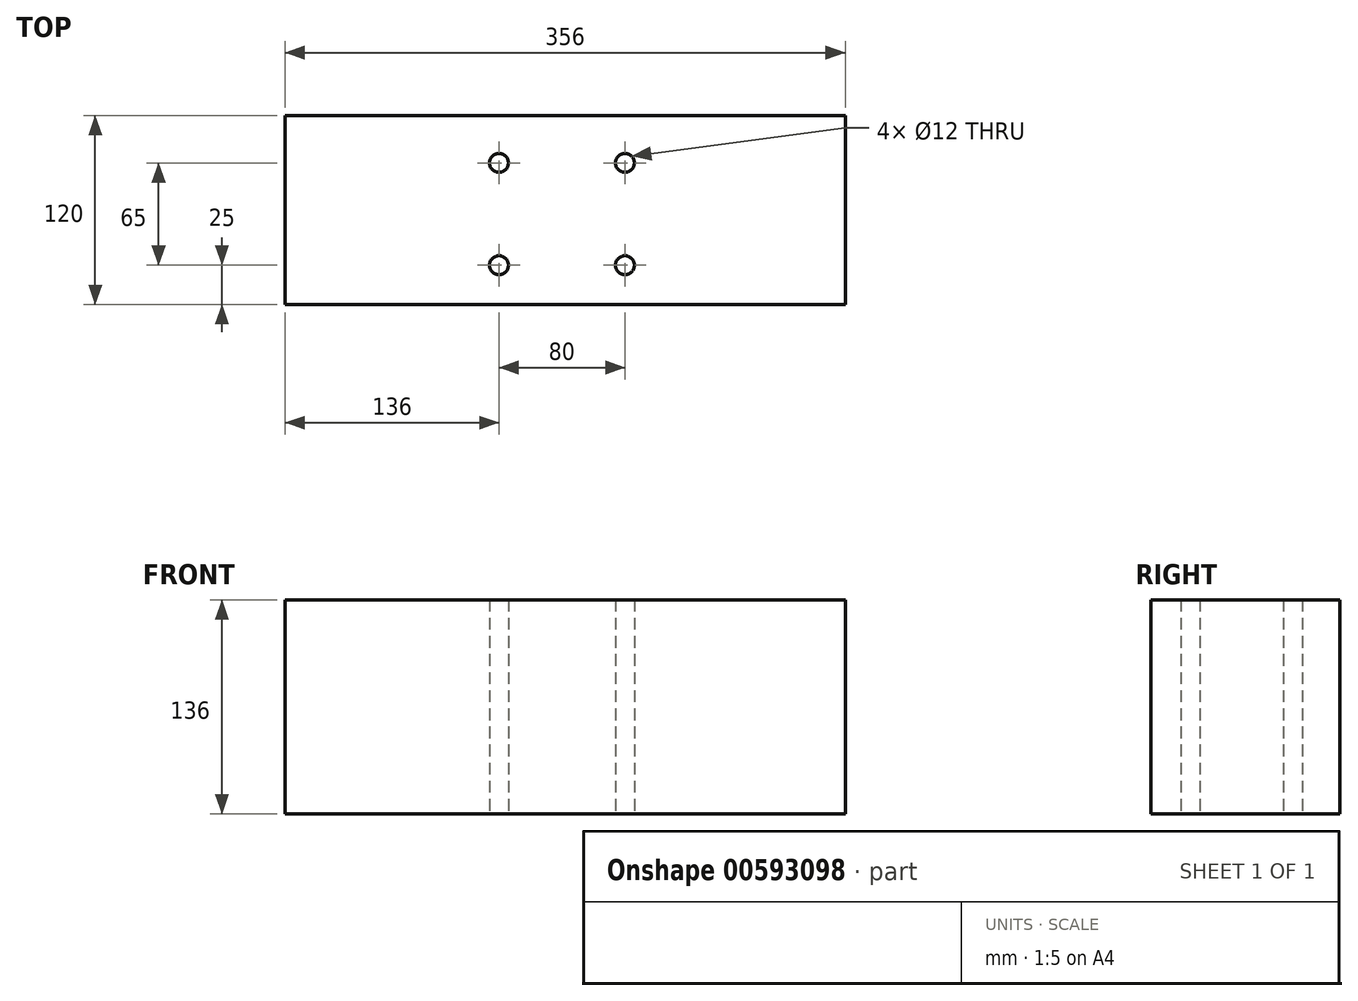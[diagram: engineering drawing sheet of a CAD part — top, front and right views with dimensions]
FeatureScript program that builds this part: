
annotation { "Feature Type Name" : "Feature", "Feature Type Description" : "" }
export const myFeature = defineFeature(function(context is Context, id is Id, definition is map)
    precondition{}
    {
        {
            var Q0;
            Q0=qCreatedBy(makeId("Top.planeOp"),FACE);
            var sketch = newSketch(context, id + "F0", { "sketchPlane" : qUnion([Q0])});
            skLineSegment(sketch, "E0.bottom", {"start": v(178, 60) * mm, "end": v(-178, 60) * mm});
            skLineSegment(sketch, "E0.top", {"start": v(178, -60) * mm, "end": v(-178, -60) * mm});
            skLineSegment(sketch, "E0.left", {"start": v(178, 60) * mm, "end": v(178, -60) * mm});
            skLineSegment(sketch, "E0.right", {"start": v(-178, 60) * mm, "end": v(-178, -60) * mm});
            skPoint(sketch, "E0.middle", {"position": v(0, 0) * mm});
            skCircle(sketch, "E1", {"center": v(-42, 30) * mm, "radius": 6 * mm});
            skCircle(sketch, "E2", {"center": v(38, 30) * mm, "radius": 6 * mm});
            skCircle(sketch, "E3", {"center": v(38, -35) * mm, "radius": 6 * mm});
            skCircle(sketch, "E4", {"center": v(-42, -35) * mm, "radius": 6 * mm});
            skSolve(sketch);
        }
        {
            var Q0;
            Q0=makeQuery(id+"F0.imprint","IMPRINT",FACE,{"disambiguationData":[TD([[makeQuery(id+"F0.imprint","IMPRINT",EDGE,{"derivedFrom":sQuery(id+"F0.wireOp",EDGE,"E0.bottom")}),1.0]])]});
            extrude(context, id + "F1", {"entities" : qUnion([Q0]), "depth" : 136 * mm, "offsetDistance" : 25 * mm});
        }
    });
